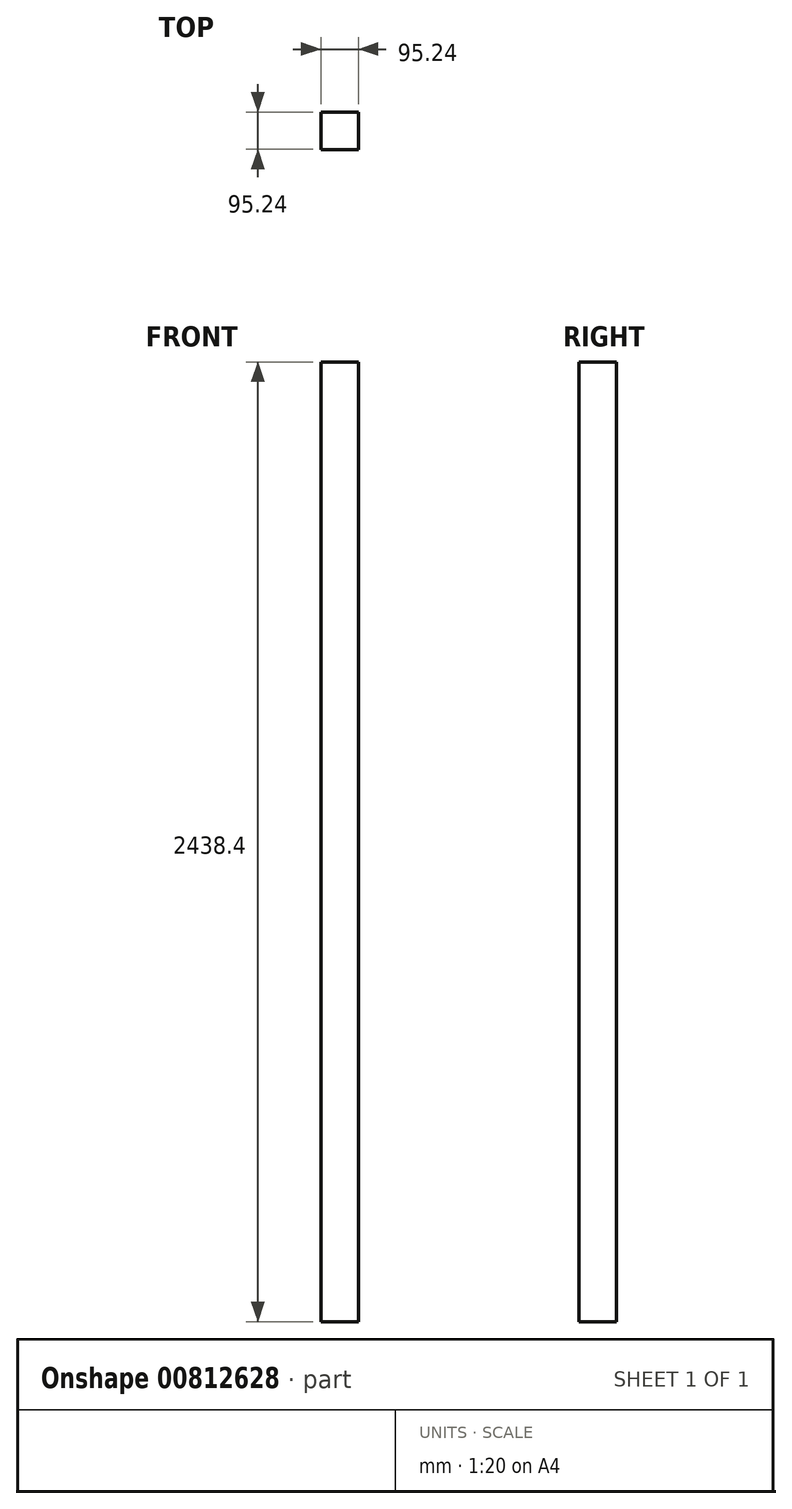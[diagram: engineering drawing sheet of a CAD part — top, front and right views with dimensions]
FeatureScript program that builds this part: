
annotation { "Feature Type Name" : "Feature", "Feature Type Description" : "" }
export const myFeature = defineFeature(function(context is Context, id is Id, definition is map)
    precondition{}
    {
        {
            var Q0;
            Q0=qCreatedBy(makeId("Top.planeOp"),FACE);
            var sketch = newSketch(context, id + "F0", { "sketchPlane" : qUnion([Q0])});
            skLineSegment(sketch, "E0.bottom", {"start": v(47.62, 47.63) * mm, "end": v(-47.63, 47.63) * mm});
            skLineSegment(sketch, "E0.top", {"start": v(47.63, -47.63) * mm, "end": v(-47.62, -47.63) * mm});
            skLineSegment(sketch, "E0.left", {"start": v(47.62, 47.63) * mm, "end": v(47.63, -47.63) * mm});
            skLineSegment(sketch, "E0.right", {"start": v(-47.63, 47.63) * mm, "end": v(-47.63, -47.63) * mm});
            skPoint(sketch, "E0.middle", {"position": v(0, 0) * mm});
            skSolve(sketch);
        }
        {
            var Q0;
            Q0 = qSketchRegion(id + "F0", true);
            extrude(context, id + "F1", {"entities" : qUnion([Q0]), "depth" : 2438.4 * mm, "offsetDistance" : 25.4 * mm});
        }
    });
